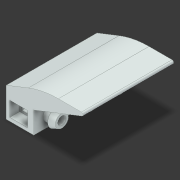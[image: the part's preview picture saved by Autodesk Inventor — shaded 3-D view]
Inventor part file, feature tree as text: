
AUTODESK INVENTOR PART (.ipt)
format: ipt  version: 2020.2 (Build 242310000, 310)  size: 296,960 bytes
history: native  units: mm
features: other x7, extrude x5, fillet x2, loft x2, pattern_linear x1
ambient origin geometry x8: Origin, YZ Plane, XZ Plane, XY Plane, X Axis, Y Axis, Z Axis, Center Point
bodies: Solid1 (feature_tree)
feature tree (17):
  other  "Start Plane"
  other  "End Plane"
  other  "Box Sketch"
  extrude  "Box"  Depth=3.0mm
  other  "Roof Sketch"
  extrude  "Roof"  Depth=2.0mm
  fillet  "Fillet1"  [1 undecoded]
  fillet  "Fillet2"  Radius=2.5mm
  extrude  "Extrusion5"  Depth=4.7625mm
  other  "Fitting"
  loft  "Loft Start Plane"
  pattern_linear  "Channel Repetition"  Spacing1=10.0mm  [1 undecoded]
  extrude  "Connector"  TaperAngle=90.0deg  [1 undecoded]
  extrude  "Extrusion3"  Depth=11.525mm
  other  "Fitting Sketch"
  loft  "Loft Sketch"
  other  "Edges1"
note: 3 required parameter values undecoded (feature->parameter linkage not recoverable at this tier; creation-order binding heuristic only, values carry confidence <= 0.55)
